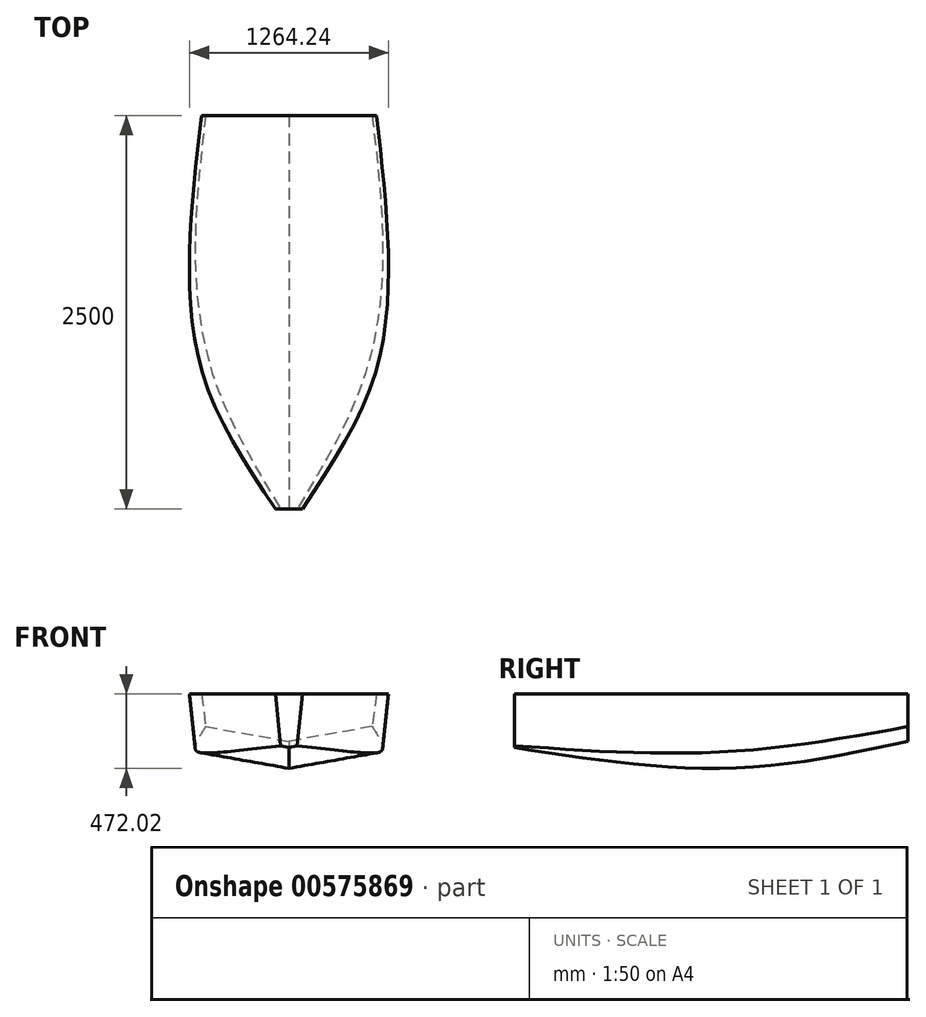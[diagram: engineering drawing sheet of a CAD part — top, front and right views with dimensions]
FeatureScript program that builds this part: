
annotation { "Feature Type Name" : "Feature", "Feature Type Description" : "" }
export const myFeature = defineFeature(function(context is Context, id is Id, definition is map)
    precondition{}
    {
        {
            var Q0;
            Q0=qCreatedBy(makeId("Front.planeOp"),FACE);
            cPlane(context, id + "F0", {"entities" : qUnion([Q0]), "cplaneType" : CPlaneType.OFFSET, "offset" : 1000 * mm, "width" : 150 * mm, "height" : 150 * mm});
        }
        {
            var Q0;
            Q0=qCreatedBy(makeId("Front.planeOp"),FACE);
            var sketch = newSketch(context, id + "F1", { "sketchPlane" : qUnion([Q0])});
            skLineSegment(sketch, "E0", {"start": v(-555.08, 0) * mm, "end": v(555.08, 0) * mm});
            skLineSegment(sketch, "E1", {"start": v(-555.08, 0) * mm, "end": v(-528.73, -206.7) * mm});
            skLineSegment(sketch, "E2", {"start": v(-528.73, -206.7) * mm, "end": v(0, -300) * mm});
            skLineSegment(sketch, "E3", {"start": v(0, -300) * mm, "end": v(0, 0) * mm, "construction": true});
            skLineSegment(sketch, "E4.MirrorCS", {"start": v(528.73, -206.7) * mm, "end": v(0, -300) * mm});
            skLineSegment(sketch, "E5.MirrorCS", {"start": v(555.08, 0) * mm, "end": v(528.73, -206.7) * mm});
            skSolve(sketch);
        }
        {
            var Q0;
            Q0=qCreatedBy(id+"F0.planeOp",FACE);
            var sketch = newSketch(context, id + "F2", { "sketchPlane" : qUnion([Q0])});
            skLineSegment(sketch, "E6", {"start": v(-632, 0) * mm, "end": v(632, 0) * mm});
            skLineSegment(sketch, "E7", {"start": v(-632, 0) * mm, "end": v(-592.6, -355) * mm});
            skLineSegment(sketch, "E8", {"start": v(-592.6, -355) * mm, "end": v(0, -464.87) * mm});
            skLineSegment(sketch, "E9", {"start": v(0, -464.87) * mm, "end": v(0, 0) * mm, "construction": true});
            skLineSegment(sketch, "E10.MirrorCS", {"start": v(592.6, -355) * mm, "end": v(0, -464.87) * mm});
            skLineSegment(sketch, "E11.MirrorCS", {"start": v(632, 0) * mm, "end": v(592.6, -355) * mm});
            skSolve(sketch);
        }
        {
            var Q0;
            Q0=qCreatedBy(makeId("Front.planeOp"),FACE);
            cPlane(context, id + "F3", {"entities" : qUnion([Q0]), "cplaneType" : CPlaneType.OFFSET, "offset" : 2500 * mm, "width" : 150 * mm, "height" : 150 * mm});
        }
        {
            var Q0;
            Q0=qCreatedBy(id+"F3.planeOp",FACE);
            var sketch = newSketch(context, id + "F4", { "sketchPlane" : qUnion([Q0])});
            skLineSegment(sketch, "E12", {"start": v(-86.17, 0) * mm, "end": v(-52.41, -327.64) * mm});
            skLineSegment(sketch, "E13", {"start": v(-52.41, -327.64) * mm, "end": v(0, -340) * mm});
            skLineSegment(sketch, "E14", {"start": v(0, -340) * mm, "end": v(0, 0) * mm, "construction": true});
            skLineSegment(sketch, "E15.MirrorCS", {"start": v(86.17, 0) * mm, "end": v(52.41, -327.64) * mm});
            skLineSegment(sketch, "E16.MirrorCS", {"start": v(52.41, -327.64) * mm, "end": v(0, -340) * mm});
            skLineSegment(sketch, "E17", {"start": v(-86.17, 0) * mm, "end": v(86.17, 0) * mm});
            skSolve(sketch);
        }
        {
            var Q0;
            Q0=qCreatedBy(id+"F0.planeOp",FACE);
            cPlane(context, id + "F5", {"entities" : qUnion([Q0]), "cplaneType" : CPlaneType.OFFSET, "offset" : 750 * mm, "width" : 150 * mm, "height" : 150 * mm});
        }
        {
            var Q0;
            Q0=qCreatedBy(id+"F5.planeOp",FACE);
            var sketch = newSketch(context, id + "F6", { "sketchPlane" : qUnion([Q0])});
            skLineSegment(sketch, "E18", {"start": v(-510.2, 0) * mm, "end": v(-446.84, -371.12) * mm});
            skLineSegment(sketch, "E19", {"start": v(-446.84, -371.12) * mm, "end": v(0, -443.1) * mm});
            skLineSegment(sketch, "E20", {"start": v(0, -443.1) * mm, "end": v(0, 0) * mm, "construction": true});
            skLineSegment(sketch, "E21.MirrorCS", {"start": v(446.84, -371.12) * mm, "end": v(0, -443.1) * mm});
            skLineSegment(sketch, "E22.MirrorCS", {"start": v(510.2, 0) * mm, "end": v(446.84, -371.12) * mm});
            skLineSegment(sketch, "E23", {"start": v(-510.2, 0) * mm, "end": v(510.2, 0) * mm});
            skSolve(sketch);
        }
        {
            var Q0;
            Q0=makeQuery(id+"F1.imprint","IMPRINT",FACE,{"disambiguationData":[TD([[makeQuery(id+"F1.imprint","IMPRINT",EDGE,{"derivedFrom":sQuery(id+"F1.wireOp",EDGE,"E0")}),-1.0]])]});
            var Q1;
            Q1=makeQuery(id+"F2.imprint","IMPRINT",FACE,{"disambiguationData":[TD([[makeQuery(id+"F2.imprint","IMPRINT",EDGE,{"derivedFrom":sQuery(id+"F2.wireOp",EDGE,"E6")}),-1.0]])]});
            var Q2;
            Q2=makeQuery(id+"F6.imprint","IMPRINT",FACE,{"disambiguationData":[TD([[makeQuery(id+"F6.imprint","IMPRINT",EDGE,{"derivedFrom":sQuery(id+"F6.wireOp",EDGE,"E18")}),1.0]])]});
            var Q3;
            Q3=makeQuery(id+"F4.imprint","IMPRINT",FACE,{"disambiguationData":[TD([[makeQuery(id+"F4.imprint","IMPRINT",EDGE,{"derivedFrom":sQuery(id+"F4.wireOp",EDGE,"E12")}),1.0]])]});
            loft(context, id + "F7", {"sheetProfilesArray" : [{ "sheetProfileEntities" : qUnion([Q0]) }, { "sheetProfileEntities" : qUnion([Q1]) }, { "sheetProfileEntities" : qUnion([Q2]) }, { "sheetProfileEntities" : qUnion([Q3]) }]});
        }
        {
            var Q0;
            Q0=qCreatedBy(makeId("Top.planeOp"),FACE);
            cPlane(context, id + "F8", {"entities" : qUnion([Q0]), "cplaneType" : CPlaneType.OFFSET, "offset" : 570 * mm, "width" : 150 * mm, "height" : 150 * mm});
        }
    });
